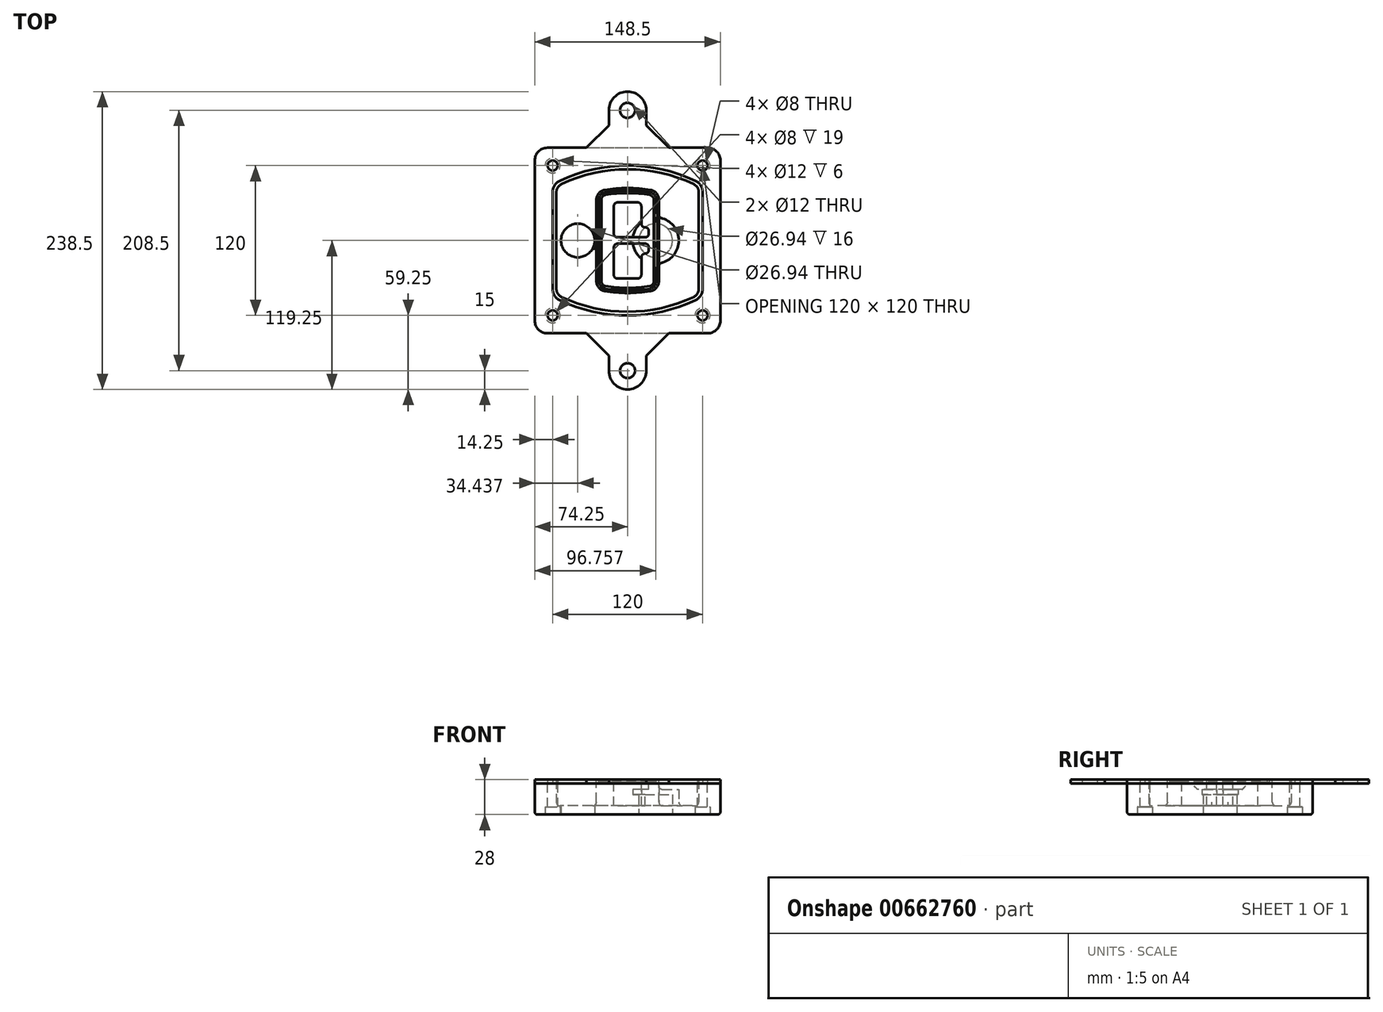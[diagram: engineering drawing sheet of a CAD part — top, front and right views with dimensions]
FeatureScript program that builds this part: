
annotation { "Feature Type Name" : "Feature", "Feature Type Description" : "" }
export const myFeature = defineFeature(function(context is Context, id is Id, definition is map)
    precondition{}
    {
        {
            var Q0;
            Q0=qCreatedBy(makeId("Top.planeOp"),FACE);
            var sketch = newSketch(context, id + "F0", { "sketchPlane" : qUnion([Q0])});
            skPoint(sketch, "E0.rect.middle", {"position": v(0, 0) * mm});
            skLineSegment(sketch, "E1.bottom", {"start": v(-64.25, -74.25) * mm, "end": v(64.25, -74.25) * mm});
            skLineSegment(sketch, "E1.top", {"start": v(-64.25, 74.25) * mm, "end": v(64.25, 74.25) * mm});
            skLineSegment(sketch, "E1.left", {"start": v(-74.25, -64.25) * mm, "end": v(-74.25, 64.25) * mm});
            skLineSegment(sketch, "E1.right", {"start": v(74.25, -64.25) * mm, "end": v(74.25, 64.25) * mm});
            skLineSegment(sketch, "E2", {"start": v(-74.25, 74.25) * mm, "end": v(74.25, -74.25) * mm, "construction": true});
            skLineSegment(sketch, "E3", {"start": v(74.25, 74.25) * mm, "end": v(-74.25, -74.25) * mm, "construction": true});
            skCircle(sketch, "E4", {"center": v(-60, 60) * mm, "radius": 4 * mm});
            skCircle(sketch, "E5", {"center": v(60, 60) * mm, "radius": 4 * mm});
            skCircle(sketch, "E6", {"center": v(60, -60) * mm, "radius": 4 * mm});
            skCircle(sketch, "E7", {"center": v(-60, -60) * mm, "radius": 4 * mm});
            skLineSegment(sketch, "E8", {"start": v(-60, 60) * mm, "end": v(60, 60) * mm, "construction": true});
            skLineSegment(sketch, "E9", {"start": v(60, 60) * mm, "end": v(60, -60) * mm, "construction": true});
            skLineSegment(sketch, "E10", {"start": v(60, -60) * mm, "end": v(-60, -60) * mm, "construction": true});
            skLineSegment(sketch, "E11", {"start": v(-60, -60) * mm, "end": v(-60, 60) * mm, "construction": true});
            skLineSegment(sketch, "E12", {"start": v(-60, 38.83) * mm, "end": v(-60, -38.83) * mm});
            skLineSegment(sketch, "E13", {"start": v(60, 38.83) * mm, "end": v(60, -38.83) * mm});
            skArc(sketch, "E14", {"start": v(54.26, 47.88) * mm, "mid": v(0, 60) * mm, "end": v(-54.26, 47.88) * mm});
            skArc(sketch, "E15", {"start": v(-54.26, -47.88) * mm, "mid": v(0, -60) * mm, "end": v(54.26, -47.88) * mm});
            skLineSegment(sketch, "E16", {"start": v(-60, 0) * mm, "end": v(60, 0) * mm, "construction": true});
            skPoint(sketch, "E17.visualSharp", {"position": v(-60, -45) * mm});
            skArc(sketch, "E17.filletArc", {"start": v(-60, -38.83) * mm, "mid": v(-58.44, -44.2) * mm, "end": v(-54.26, -47.88) * mm});
            skPoint(sketch, "E18.visualSharp", {"position": v(-60, 45) * mm});
            skArc(sketch, "E18.filletArc", {"start": v(-54.26, 47.88) * mm, "mid": v(-58.44, 44.2) * mm, "end": v(-60, 38.83) * mm});
            skPoint(sketch, "E19.visualSharp", {"position": v(60, 45) * mm});
            skArc(sketch, "E19.filletArc", {"start": v(60, 38.83) * mm, "mid": v(58.44, 44.2) * mm, "end": v(54.26, 47.88) * mm});
            skPoint(sketch, "E20.visualSharp", {"position": v(60, -45) * mm});
            skArc(sketch, "E20.filletArc", {"start": v(54.26, -47.88) * mm, "mid": v(58.44, -44.2) * mm, "end": v(60, -38.83) * mm});
            skPoint(sketch, "E21.visualSharp", {"position": v(-74.25, 74.25) * mm});
            skArc(sketch, "E21.filletArc", {"start": v(-64.25, 74.25) * mm, "mid": v(-71.32, 71.32) * mm, "end": v(-74.25, 64.25) * mm});
            skPoint(sketch, "E22.visualSharp", {"position": v(74.25, 74.25) * mm});
            skArc(sketch, "E22.filletArc", {"start": v(74.25, 64.25) * mm, "mid": v(71.32, 71.32) * mm, "end": v(64.25, 74.25) * mm});
            skPoint(sketch, "E23.visualSharp", {"position": v(74.25, -74.25) * mm});
            skArc(sketch, "E23.filletArc", {"start": v(64.25, -74.25) * mm, "mid": v(71.32, -71.32) * mm, "end": v(74.25, -64.25) * mm});
            skPoint(sketch, "E24.visualSharp", {"position": v(-74.25, -74.25) * mm});
            skArc(sketch, "E24.filletArc", {"start": v(-74.25, -64.25) * mm, "mid": v(-71.32, -71.32) * mm, "end": v(-64.25, -74.25) * mm});
            skArc(sketch, "E25.0", {"start": v(57, 38.83) * mm, "mid": v(55.9, 42.58) * mm, "end": v(52.98, 45.17) * mm});
            skLineSegment(sketch, "E25.1", {"start": v(57, 38.83) * mm, "end": v(57, -38.83) * mm});
            skArc(sketch, "E25.2", {"start": v(52.98, -45.17) * mm, "mid": v(55.9, -42.58) * mm, "end": v(57, -38.83) * mm});
            skArc(sketch, "E25.3", {"start": v(-52.98, -45.17) * mm, "mid": v(0, -57) * mm, "end": v(52.98, -45.17) * mm});
            skArc(sketch, "E25.4", {"start": v(-57, -38.83) * mm, "mid": v(-55.9, -42.58) * mm, "end": v(-52.98, -45.17) * mm});
            skArc(sketch, "E25.5", {"start": v(52.98, 45.17) * mm, "mid": v(0, 57) * mm, "end": v(-52.98, 45.17) * mm});
            skLineSegment(sketch, "E25.6", {"start": v(-57, 38.83) * mm, "end": v(-57, -38.83) * mm});
            skArc(sketch, "E25.7", {"start": v(-52.98, 45.17) * mm, "mid": v(-55.9, 42.58) * mm, "end": v(-57, 38.83) * mm});
            skArc(sketch, "E26.0", {"start": v(-55.96, 51.5) * mm, "mid": v(-61.82, 46.33) * mm, "end": v(-64, 38.83) * mm});
            skArc(sketch, "E26.1", {"start": v(55.96, 51.5) * mm, "mid": v(0, 64) * mm, "end": v(-55.96, 51.5) * mm});
            skArc(sketch, "E26.2", {"start": v(64, 38.83) * mm, "mid": v(61.82, 46.33) * mm, "end": v(55.96, 51.5) * mm});
            skLineSegment(sketch, "E26.3", {"start": v(64, 38.83) * mm, "end": v(64, -38.83) * mm});
            skArc(sketch, "E26.4", {"start": v(55.96, -51.5) * mm, "mid": v(61.82, -46.33) * mm, "end": v(64, -38.83) * mm});
            skLineSegment(sketch, "E26.5", {"start": v(-64, 38.83) * mm, "end": v(-64, -38.83) * mm});
            skArc(sketch, "E26.6", {"start": v(-55.96, -51.5) * mm, "mid": v(0, -64) * mm, "end": v(55.96, -51.5) * mm});
            skArc(sketch, "E26.7", {"start": v(-64, -38.83) * mm, "mid": v(-61.82, -46.33) * mm, "end": v(-55.96, -51.5) * mm});
            skSolve(sketch);
        }
        {
            var Q0;
            Q0=makeQuery(id+"F0.imprint","IMPRINT",FACE,{"disambiguationData":[TD([[makeQuery(id+"F0.imprint","IMPRINT",EDGE,{"derivedFrom":sQuery(id+"F0.wireOp",EDGE,"E1.bottom")}),1.0]])]});
            var Q1;
            Q1=makeQuery(id+"F0.imprint","IMPRINT",FACE,{"disambiguationData":[TD([[makeQuery(id+"F0.imprint","IMPRINT",EDGE,{"derivedFrom":sQuery(id+"F0.wireOp",EDGE,"E12")}),1.0]])]});
            var Q2;
            Q2=makeQuery(id+"F0.imprint","IMPRINT",FACE,{"disambiguationData":[TD([[makeQuery(id+"F0.imprint","IMPRINT",EDGE,{"derivedFrom":sQuery(id+"F0.wireOp",EDGE,"E25.0")}),1.0]])]});
            var Q3;
            Q3=makeQuery(id+"F0.imprint","IMPRINT",FACE,{"disambiguationData":[TD([[makeQuery(id+"F0.imprint","IMPRINT",EDGE,{"derivedFrom":sQuery(id+"F0.wireOp",EDGE,"E12")}),-1.0]])]});
            extrude(context, id + "F1", {"entities" : qUnion([Q0, Q1, Q2, Q3]), "oppositeDirection" : true, "depth" : 25 * mm});
        }
        {
            var Q0;
            Q0=makeQuery(id+"F0.imprint","IMPRINT",FACE,{"disambiguationData":[TD([[makeQuery(id+"F0.imprint","IMPRINT",EDGE,{"derivedFrom":sQuery(id+"F0.wireOp",EDGE,"E12")}),1.0]])]});
            extrude(context, id + "F2", {"entities" : qUnion([Q0]), "operationType" : NewBodyOperationType.ADD, "depth" : 3 * mm});
        }
        {
            var Q0;
            Q0=makeQuery(id+"F0.imprint","IMPRINT",FACE,{"disambiguationData":[TD([[makeQuery(id+"F0.imprint","IMPRINT",EDGE,{"derivedFrom":sQuery(id+"F0.wireOp",EDGE,"E25.0")}),1.0]])]});
            extrude(context, id + "F3", {"entities" : qUnion([Q0]), "operationType" : NewBodyOperationType.REMOVE, "oppositeDirection" : true, "depth" : 18 * mm});
        }
        {
            var Q0;
            Q0=makeQuery(id+"F2.opExtrude","CAP_FACE",FACE,{"disambiguationData":[OSD([sQuery(id+"F0.wireOp",EDGE,"E12"),sQuery(id+"F0.wireOp",EDGE,"E13"),sQuery(id+"F0.wireOp",EDGE,"E14"),sQuery(id+"F0.wireOp",EDGE,"E15"),sQuery(id+"F0.wireOp",EDGE,"E17.filletArc"),sQuery(id+"F0.wireOp",EDGE,"E18.filletArc"),sQuery(id+"F0.wireOp",EDGE,"E19.filletArc"),sQuery(id+"F0.wireOp",EDGE,"E20.filletArc"),sQuery(id+"F0.wireOp",EDGE,"E25.0"),sQuery(id+"F0.wireOp",EDGE,"E25.1"),sQuery(id+"F0.wireOp",EDGE,"E25.2"),sQuery(id+"F0.wireOp",EDGE,"E25.3"),sQuery(id+"F0.wireOp",EDGE,"E25.4"),sQuery(id+"F0.wireOp",EDGE,"E25.5"),sQuery(id+"F0.wireOp",EDGE,"E25.6"),sQuery(id+"F0.wireOp",EDGE,"E25.7")])],"isStart":false});
            var sketch = newSketch(context, id + "F4", { "sketchPlane" : qUnion([Q0])});
            skArc(sketch, "E27.0", {"start": v(-18.34, -40.45) * mm, "mid": v(0, -42) * mm, "end": v(18.34, -40.45) * mm});
            skArc(sketch, "E28.0", {"start": v(18.34, 40.45) * mm, "mid": v(0, 42) * mm, "end": v(-18.34, 40.45) * mm});
            skLineSegment(sketch, "E29", {"start": v(-25, 32.57) * mm, "end": v(-25, -32.57) * mm});
            skLineSegment(sketch, "E30", {"start": v(25, 32.57) * mm, "end": v(25, -32.57) * mm});
            skLineSegment(sketch, "E31", {"start": v(-25, 39.1) * mm, "end": v(25, 39.1) * mm, "construction": true});
            skLineSegment(sketch, "E32", {"start": v(-25, -39.1) * mm, "end": v(25, -39.1) * mm, "construction": true});
            skPoint(sketch, "E33.visualSharp", {"position": v(-25, 39.1) * mm});
            skArc(sketch, "E33.filletArc", {"start": v(-18.34, 40.45) * mm, "mid": v(-23.11, 37.73) * mm, "end": v(-25, 32.57) * mm});
            skPoint(sketch, "E34.visualSharp", {"position": v(25, 39.1) * mm});
            skArc(sketch, "E34.filletArc", {"start": v(25, 32.57) * mm, "mid": v(23.11, 37.73) * mm, "end": v(18.34, 40.45) * mm});
            skPoint(sketch, "E35.visualSharp", {"position": v(25, -39.1) * mm});
            skArc(sketch, "E35.filletArc", {"start": v(18.34, -40.45) * mm, "mid": v(23.11, -37.73) * mm, "end": v(25, -32.57) * mm});
            skPoint(sketch, "E36.visualSharp", {"position": v(-25, -39.1) * mm});
            skArc(sketch, "E36.filletArc", {"start": v(-25, -32.57) * mm, "mid": v(-23.11, -37.73) * mm, "end": v(-18.34, -40.45) * mm});
            skArc(sketch, "E37.0", {"start": v(52.98, 45.17) * mm, "mid": v(0, 57) * mm, "end": v(-52.98, 45.17) * mm});
            skArc(sketch, "E37.1", {"start": v(-52.98, 45.17) * mm, "mid": v(-55.9, 42.58) * mm, "end": v(-57, 38.83) * mm});
            skLineSegment(sketch, "E37.2", {"start": v(-57, 38.83) * mm, "end": v(-57, -38.83) * mm});
            skArc(sketch, "E37.3", {"start": v(-57, -38.83) * mm, "mid": v(-55.9, -42.58) * mm, "end": v(-52.98, -45.17) * mm});
            skArc(sketch, "E37.4", {"start": v(-52.98, -45.17) * mm, "mid": v(0, -57) * mm, "end": v(52.98, -45.17) * mm});
            skArc(sketch, "E37.5", {"start": v(52.98, -45.17) * mm, "mid": v(55.9, -42.58) * mm, "end": v(57, -38.83) * mm});
            skLineSegment(sketch, "E37.6", {"start": v(57, 38.83) * mm, "end": v(57, -38.83) * mm});
            skArc(sketch, "E37.7", {"start": v(57, 38.83) * mm, "mid": v(55.9, 42.58) * mm, "end": v(52.98, 45.17) * mm});
            skLineSegment(sketch, "E38.0", {"start": v(23, 32.57) * mm, "end": v(23, -32.57) * mm});
            skArc(sketch, "E38.1", {"start": v(18, -38.48) * mm, "mid": v(21.58, -36.44) * mm, "end": v(23, -32.57) * mm});
            skArc(sketch, "E38.2", {"start": v(-18, -38.48) * mm, "mid": v(0, -40) * mm, "end": v(18, -38.48) * mm});
            skArc(sketch, "E38.3", {"start": v(-23, -32.57) * mm, "mid": v(-21.58, -36.44) * mm, "end": v(-18, -38.48) * mm});
            skLineSegment(sketch, "E38.4", {"start": v(-23, 32.57) * mm, "end": v(-23, -32.57) * mm});
            skArc(sketch, "E38.5", {"start": v(23, 32.57) * mm, "mid": v(21.58, 36.44) * mm, "end": v(18, 38.48) * mm});
            skArc(sketch, "E38.6", {"start": v(-18, 38.48) * mm, "mid": v(-21.58, 36.44) * mm, "end": v(-23, 32.57) * mm});
            skArc(sketch, "E38.7", {"start": v(18, 38.48) * mm, "mid": v(0, 40) * mm, "end": v(-18, 38.48) * mm});
            skArc(sketch, "E39.0", {"start": v(21, 32.57) * mm, "mid": v(20.06, 35.15) * mm, "end": v(17.67, 36.5) * mm});
            skLineSegment(sketch, "E39.1", {"start": v(21, 32.57) * mm, "end": v(21, -32.57) * mm});
            skArc(sketch, "E39.2", {"start": v(17.67, -36.5) * mm, "mid": v(20.06, -35.15) * mm, "end": v(21, -32.57) * mm});
            skArc(sketch, "E39.3", {"start": v(-17.67, -36.5) * mm, "mid": v(0, -38) * mm, "end": v(17.67, -36.5) * mm});
            skArc(sketch, "E39.4", {"start": v(-21, -32.57) * mm, "mid": v(-20.06, -35.15) * mm, "end": v(-17.67, -36.5) * mm});
            skArc(sketch, "E39.5", {"start": v(17.67, 36.5) * mm, "mid": v(0, 38) * mm, "end": v(-17.67, 36.5) * mm});
            skLineSegment(sketch, "E39.6", {"start": v(-21, 32.57) * mm, "end": v(-21, -32.57) * mm});
            skArc(sketch, "E39.7", {"start": v(-17.67, 36.5) * mm, "mid": v(-20.06, 35.15) * mm, "end": v(-21, 32.57) * mm});
            skLineSegment(sketch, "E40", {"start": v(-25, 0) * mm, "end": v(25, 0) * mm, "construction": true});
            skLineSegment(sketch, "E41", {"start": v(-11, 5.5) * mm, "end": v(-11, 27.5) * mm});
            skLineSegment(sketch, "E42", {"start": v(-8, 30.5) * mm, "end": v(8, 30.5) * mm});
            skLineSegment(sketch, "E43", {"start": v(11, 27.5) * mm, "end": v(11, 13.5) * mm});
            skLineSegment(sketch, "E44", {"start": v(14, 10.5) * mm, "end": v(14, 10.5) * mm});
            skLineSegment(sketch, "E45", {"start": v(17, 7.5) * mm, "end": v(17, 5.5) * mm});
            skLineSegment(sketch, "E46", {"start": v(14, 2.5) * mm, "end": v(-8, 2.5) * mm});
            skPoint(sketch, "E47.visualSharp", {"position": v(-11, 30.5) * mm});
            skArc(sketch, "E47.filletArc", {"start": v(-8, 30.5) * mm, "mid": v(-10.12, 29.62) * mm, "end": v(-11, 27.5) * mm});
            skPoint(sketch, "E48.visualSharp", {"position": v(11, 30.5) * mm});
            skArc(sketch, "E48.filletArc", {"start": v(11, 27.5) * mm, "mid": v(10.12, 29.62) * mm, "end": v(8, 30.5) * mm});
            skPoint(sketch, "E49.visualSharp", {"position": v(11, 10.5) * mm});
            skArc(sketch, "E49.filletArc", {"start": v(11, 13.5) * mm, "mid": v(11.88, 11.38) * mm, "end": v(14, 10.5) * mm});
            skPoint(sketch, "E50.visualSharp", {"position": v(17, 10.5) * mm});
            skArc(sketch, "E50.filletArc", {"start": v(17, 7.5) * mm, "mid": v(16.12, 9.62) * mm, "end": v(14, 10.5) * mm});
            skPoint(sketch, "E51.visualSharp", {"position": v(17, 2.5) * mm});
            skArc(sketch, "E51.filletArc", {"start": v(14, 2.5) * mm, "mid": v(16.12, 3.38) * mm, "end": v(17, 5.5) * mm});
            skPoint(sketch, "E52.visualSharp", {"position": v(-11, 2.5) * mm});
            skArc(sketch, "E52.filletArc", {"start": v(-11, 5.5) * mm, "mid": v(-10.12, 3.38) * mm, "end": v(-8, 2.5) * mm});
            skLineSegment(sketch, "E53.0.MirrorCS", {"start": v(14, -2.5) * mm, "end": v(-8, -2.5) * mm});
            skArc(sketch, "E54.0.MirrorCS", {"start": v(-11, -5.5) * mm, "mid": v(-10.12, -3.38) * mm, "end": v(-8, -2.5) * mm});
            skLineSegment(sketch, "E55.0.MirrorCS", {"start": v(-11, -5.5) * mm, "end": v(-11, -27.5) * mm});
            skArc(sketch, "E56.0.MirrorCS", {"start": v(-8, -30.5) * mm, "mid": v(-10.12, -29.62) * mm, "end": v(-11, -27.5) * mm});
            skLineSegment(sketch, "E57.0.MirrorCS", {"start": v(-8, -30.5) * mm, "end": v(8, -30.5) * mm});
            skArc(sketch, "E58.0.MirrorCS", {"start": v(11, -27.5) * mm, "mid": v(10.12, -29.62) * mm, "end": v(8, -30.5) * mm});
            skLineSegment(sketch, "E59.0.MirrorCS", {"start": v(11, -27.5) * mm, "end": v(11, -13.5) * mm});
            skArc(sketch, "E60.0.MirrorCS", {"start": v(11, -13.5) * mm, "mid": v(11.88, -11.38) * mm, "end": v(14, -10.5) * mm});
            skArc(sketch, "E61.0.MirrorCS", {"start": v(17, -7.5) * mm, "mid": v(16.12, -9.62) * mm, "end": v(14, -10.5) * mm});
            skLineSegment(sketch, "E62.0.MirrorCS", {"start": v(17, -7.5) * mm, "end": v(17, -5.5) * mm});
            skArc(sketch, "E63.0.MirrorCS", {"start": v(14, -2.5) * mm, "mid": v(16.12, -3.38) * mm, "end": v(17, -5.5) * mm});
            skSolve(sketch);
        }
        {
            var Q0;
            Q0=makeQuery(id+"F4.imprint","IMPRINT",FACE,{"disambiguationData":[TD([[makeQuery(id+"F4.imprint","IMPRINT",EDGE,{"derivedFrom":sQuery(id+"F4.wireOp",EDGE,"E27.0")}),1.0]])]});
            var Q1;
            Q1=makeQuery(id+"F4.imprint","IMPRINT",FACE,{"disambiguationData":[TD([[makeQuery(id+"F4.imprint","IMPRINT",EDGE,{"derivedFrom":sQuery(id+"F4.wireOp",EDGE,"E38.0")}),-1.0]])]});
            var Q2;
            Q2=makeQuery(id+"F4.imprint","IMPRINT",FACE,{"disambiguationData":[TD([[makeQuery(id+"F4.imprint","IMPRINT",EDGE,{"derivedFrom":sQuery(id+"F4.wireOp",EDGE,"E39.0")}),1.0]])]});
            extrude(context, id + "F5", {"entities" : qUnion([Q0, Q1, Q2]), "operationType" : NewBodyOperationType.ADD, "endBound" : BoundingType.UP_TO_NEXT, "oppositeDirection" : true, "depth" : 25 * mm});
        }
        {
            var Q0;
            Q0=makeQuery(id+"F4.imprint","IMPRINT",FACE,{"disambiguationData":[TD([[makeQuery(id+"F4.imprint","IMPRINT",EDGE,{"derivedFrom":sQuery(id+"F4.wireOp",EDGE,"E38.0")}),-1.0]])]});
            extrude(context, id + "F6", {"entities" : qUnion([Q0]), "operationType" : NewBodyOperationType.REMOVE, "oppositeDirection" : true, "depth" : 2 * mm});
        }
        {
            var Q0;
            Q0=makeQuery(id+"F1.opExtrude","CAP_FACE",FACE,{"disambiguationData":[OSD([sQuery(id+"F0.wireOp",EDGE,"E1.bottom"),sQuery(id+"F0.wireOp",EDGE,"E1.top"),sQuery(id+"F0.wireOp",EDGE,"E1.left"),sQuery(id+"F0.wireOp",EDGE,"E1.right"),sQuery(id+"F0.wireOp",EDGE,"E4"),sQuery(id+"F0.wireOp",EDGE,"E5"),sQuery(id+"F0.wireOp",EDGE,"E6"),sQuery(id+"F0.wireOp",EDGE,"E7"),sQuery(id+"F0.wireOp",EDGE,"E21.filletArc"),sQuery(id+"F0.wireOp",EDGE,"E22.filletArc"),sQuery(id+"F0.wireOp",EDGE,"E23.filletArc"),sQuery(id+"F0.wireOp",EDGE,"E24.filletArc")])],"isStart":false});
            var sketch = newSketch(context, id + "F7", { "sketchPlane" : qUnion([Q0])});
            skCircle(sketch, "E64", {"center": v(22.5, 0) * mm, "radius": 13.47 * mm});
            skCircle(sketch, "E65", {"center": v(-39.81, 0) * mm, "radius": 13.47 * mm});
            skLineSegment(sketch, "E66", {"start": v(74.25, 0) * mm, "end": v(-74.25, 0) * mm});
            skCircle(sketch, "E67", {"center": v(22.5, 0) * mm, "radius": 18.47 * mm});
            skCircle(sketch, "E68", {"center": v(60, -60) * mm, "radius": 6 * mm});
            skCircle(sketch, "E69", {"center": v(-60, -60) * mm, "radius": 6 * mm});
            skCircle(sketch, "E70", {"center": v(-60, 60) * mm, "radius": 6 * mm});
            skCircle(sketch, "E71", {"center": v(60, 60) * mm, "radius": 6 * mm});
            skSolve(sketch);
        }
        {
            var Q0;
            {var subQ1=sQuery(id+"F7.wireOp",EDGE,"E66");var subQ4=sQuery(id+"F7.wireOp",EDGE,"E64");var subQ6=makeQuery(id+"F7.imprint","INTERSECT",VERTEX,{"disambiguationData":[OD(0.0)],"derivedFrom":[subQ4,subQ1]});Q0=makeQuery(id+"F7.imprint","IMPRINT",FACE,{"disambiguationData":[TD([[makeQuery(id+"F7.imprint","IMPRINT",EDGE,{"disambiguationData":[TD([[subQ6,-1.0]])],"derivedFrom":subQ4}),-1.0]])]});}
            var Q1;
            {var subQ0=sQuery(id+"F7.wireOp",EDGE,"E66");var subQ1=sQuery(id+"F7.wireOp",EDGE,"E64");var subQ3=makeQuery(id+"F7.imprint","INTERSECT",VERTEX,{"disambiguationData":[OD(0.0)],"derivedFrom":[subQ1,subQ0]});Q1=makeQuery(id+"F7.imprint","IMPRINT",FACE,{"disambiguationData":[TD([[makeQuery(id+"F7.imprint","IMPRINT",EDGE,{"disambiguationData":[TD([[subQ3,-1.0]])],"derivedFrom":subQ1}),1.0]])]});}
            var Q2;
            {var subQ0=sQuery(id+"F7.wireOp",EDGE,"E66");var subQ1=sQuery(id+"F7.wireOp",EDGE,"E64");var subQ3=makeQuery(id+"F7.imprint","INTERSECT",VERTEX,{"disambiguationData":[OD(0.0)],"derivedFrom":[subQ1,subQ0]});Q2=makeQuery(id+"F7.imprint","IMPRINT",FACE,{"disambiguationData":[TD([[makeQuery(id+"F7.imprint","IMPRINT",EDGE,{"disambiguationData":[TD([[subQ3,1.0]])],"derivedFrom":subQ1}),1.0]])]});}
            var Q3;
            {var subQ1=sQuery(id+"F7.wireOp",EDGE,"E66");var subQ4=sQuery(id+"F7.wireOp",EDGE,"E64");var subQ6=makeQuery(id+"F7.imprint","INTERSECT",VERTEX,{"disambiguationData":[OD(0.0)],"derivedFrom":[subQ4,subQ1]});Q3=makeQuery(id+"F7.imprint","IMPRINT",FACE,{"disambiguationData":[TD([[makeQuery(id+"F7.imprint","IMPRINT",EDGE,{"disambiguationData":[TD([[subQ6,1.0]])],"derivedFrom":subQ4}),-1.0]])]});}
            extrude(context, id + "F8", {"entities" : qUnion([Q0, Q1, Q2, Q3]), "operationType" : NewBodyOperationType.ADD, "oppositeDirection" : true, "depth" : 20 * mm});
        }
        {
            var Q0;
            {var subQ0=sQuery(id+"F7.wireOp",EDGE,"E66");var subQ1=sQuery(id+"F7.wireOp",EDGE,"E64");var subQ3=makeQuery(id+"F7.imprint","INTERSECT",VERTEX,{"disambiguationData":[OD(0.0)],"derivedFrom":[subQ1,subQ0]});Q0=makeQuery(id+"F7.imprint","IMPRINT",FACE,{"disambiguationData":[TD([[makeQuery(id+"F7.imprint","IMPRINT",EDGE,{"disambiguationData":[TD([[subQ3,-1.0]])],"derivedFrom":subQ1}),1.0]])]});}
            var Q1;
            {var subQ0=sQuery(id+"F7.wireOp",EDGE,"E66");var subQ1=sQuery(id+"F7.wireOp",EDGE,"E64");var subQ3=makeQuery(id+"F7.imprint","INTERSECT",VERTEX,{"disambiguationData":[OD(0.0)],"derivedFrom":[subQ1,subQ0]});Q1=makeQuery(id+"F7.imprint","IMPRINT",FACE,{"disambiguationData":[TD([[makeQuery(id+"F7.imprint","IMPRINT",EDGE,{"disambiguationData":[TD([[subQ3,1.0]])],"derivedFrom":subQ1}),1.0]])]});}
            extrude(context, id + "F9", {"entities" : qUnion([Q0, Q1]), "operationType" : NewBodyOperationType.REMOVE, "oppositeDirection" : true, "depth" : 16 * mm});
        }
        {
            var Q0;
            {var subQ0=sQuery(id+"F7.wireOp",EDGE,"E66");var subQ1=sQuery(id+"F7.wireOp",EDGE,"E65");var subQ3=makeQuery(id+"F7.imprint","INTERSECT",VERTEX,{"disambiguationData":[OD(0.0)],"derivedFrom":[subQ1,subQ0]});Q0=makeQuery(id+"F7.imprint","IMPRINT",FACE,{"disambiguationData":[TD([[makeQuery(id+"F7.imprint","IMPRINT",EDGE,{"disambiguationData":[TD([[subQ3,-1.0]])],"derivedFrom":subQ1}),1.0]])]});}
            var Q1;
            {var subQ0=sQuery(id+"F7.wireOp",EDGE,"E66");var subQ1=sQuery(id+"F7.wireOp",EDGE,"E65");var subQ3=makeQuery(id+"F7.imprint","INTERSECT",VERTEX,{"disambiguationData":[OD(0.0)],"derivedFrom":[subQ1,subQ0]});Q1=makeQuery(id+"F7.imprint","IMPRINT",FACE,{"disambiguationData":[TD([[makeQuery(id+"F7.imprint","IMPRINT",EDGE,{"disambiguationData":[TD([[subQ3,1.0]])],"derivedFrom":subQ1}),1.0]])]});}
            extrude(context, id + "F10", {"entities" : qUnion([Q0, Q1]), "operationType" : NewBodyOperationType.REMOVE, "oppositeDirection" : true, "depth" : 25 * mm});
        }
        {
            var Q0;
            Q0=makeQuery(id+"F7.imprint","IMPRINT",FACE,{"disambiguationData":[TD([[makeQuery(id+"F7.imprint","IMPRINT",EDGE,{"derivedFrom":sQuery(id+"F7.wireOp",EDGE,"E68")}),1.0]])]});
            var Q1;
            Q1=makeQuery(id+"F7.imprint","IMPRINT",FACE,{"disambiguationData":[TD([[makeQuery(id+"F7.imprint","IMPRINT",EDGE,{"derivedFrom":makeQuery(id+"F1.opExtrude","CAP_EDGE",EDGE,{"disambiguationData":[OSD([sQuery(id+"F0.wireOp",EDGE,"E5")])],"isStart":false})}),-1.0]])]});
            var Q2;
            Q2=makeQuery(id+"F7.imprint","IMPRINT",FACE,{"disambiguationData":[TD([[makeQuery(id+"F7.imprint","IMPRINT",EDGE,{"derivedFrom":sQuery(id+"F7.wireOp",EDGE,"E69")}),1.0]])]});
            var Q3;
            Q3=makeQuery(id+"F7.imprint","IMPRINT",FACE,{"disambiguationData":[TD([[makeQuery(id+"F7.imprint","IMPRINT",EDGE,{"derivedFrom":makeQuery(id+"F1.opExtrude","CAP_EDGE",EDGE,{"disambiguationData":[OSD([sQuery(id+"F0.wireOp",EDGE,"E4")])],"isStart":false})}),-1.0]])]});
            var Q4;
            Q4=makeQuery(id+"F7.imprint","IMPRINT",FACE,{"disambiguationData":[TD([[makeQuery(id+"F7.imprint","IMPRINT",EDGE,{"derivedFrom":sQuery(id+"F7.wireOp",EDGE,"E70")}),1.0]])]});
            var Q5;
            Q5=makeQuery(id+"F7.imprint","IMPRINT",FACE,{"disambiguationData":[TD([[makeQuery(id+"F7.imprint","IMPRINT",EDGE,{"derivedFrom":makeQuery(id+"F1.opExtrude","CAP_EDGE",EDGE,{"disambiguationData":[OSD([sQuery(id+"F0.wireOp",EDGE,"E7")])],"isStart":false})}),-1.0]])]});
            var Q6;
            Q6=makeQuery(id+"F7.imprint","IMPRINT",FACE,{"disambiguationData":[TD([[makeQuery(id+"F7.imprint","IMPRINT",EDGE,{"derivedFrom":sQuery(id+"F7.wireOp",EDGE,"E71")}),1.0]])]});
            var Q7;
            Q7=makeQuery(id+"F7.imprint","IMPRINT",FACE,{"disambiguationData":[TD([[makeQuery(id+"F7.imprint","IMPRINT",EDGE,{"derivedFrom":makeQuery(id+"F1.opExtrude","CAP_EDGE",EDGE,{"disambiguationData":[OSD([sQuery(id+"F0.wireOp",EDGE,"E6")])],"isStart":false})}),-1.0]])]});
            extrude(context, id + "F11", {"entities" : qUnion([Q0, Q1, Q2, Q3, Q4, Q5, Q6, Q7]), "operationType" : NewBodyOperationType.REMOVE, "oppositeDirection" : true, "depth" : 6 * mm});
        }
        {
            var Q0;
            Q0=makeQuery(id+"F9.boolean.opBoolean","COPY",FACE,{"derivedFrom":makeQuery(id+"F9.opExtrude","CAP_FACE",FACE,{"disambiguationData":[OSD([sQuery(id+"F7.wireOp",EDGE,"E64")])],"isStart":false})});
            var sketch = newSketch(context, id + "F12", { "sketchPlane" : qUnion([Q0])});
            skArc(sketch, "E72.0", {"start": v(11, 14.45) * mm, "mid": v(6.45, 9.13) * mm, "end": v(4.2, 2.5) * mm});
            skArc(sketch, "E72.1", {"start": v(4.2, -2.5) * mm, "mid": v(6.45, -9.13) * mm, "end": v(11, -14.45) * mm});
            skLineSegment(sketch, "E73", {"start": v(4.2, -2.5) * mm, "end": v(14, -2.5) * mm});
            skLineSegment(sketch, "E74.0", {"start": v(14, 2.5) * mm, "end": v(4.2, 2.5) * mm});
            skArc(sketch, "E74.1", {"start": v(14, 2.5) * mm, "mid": v(16.12, 3.38) * mm, "end": v(17, 5.5) * mm});
            skLineSegment(sketch, "E74.2", {"start": v(17, 7.5) * mm, "end": v(17, 5.5) * mm});
            skArc(sketch, "E74.3", {"start": v(17, 7.5) * mm, "mid": v(16.12, 9.62) * mm, "end": v(14, 10.5) * mm});
            skArc(sketch, "E74.4", {"start": v(11, 13.5) * mm, "mid": v(11.88, 11.38) * mm, "end": v(14, 10.5) * mm});
            skLineSegment(sketch, "E74.5", {"start": v(11, 14.45) * mm, "end": v(11, 13.5) * mm});
            skLineSegment(sketch, "E74.7", {"start": v(14, -2.5) * mm, "end": v(4.2, -2.5) * mm});
            skArc(sketch, "E74.8", {"start": v(14, -2.5) * mm, "mid": v(16.12, -3.38) * mm, "end": v(17, -5.5) * mm});
            skLineSegment(sketch, "E74.9", {"start": v(17, -7.5) * mm, "end": v(17, -5.5) * mm});
            skArc(sketch, "E74.10", {"start": v(17, -7.5) * mm, "mid": v(16.12, -9.62) * mm, "end": v(14, -10.5) * mm});
            skArc(sketch, "E74.11", {"start": v(11, -13.5) * mm, "mid": v(11.88, -11.38) * mm, "end": v(14, -10.5) * mm});
            skLineSegment(sketch, "E74.12", {"start": v(11, -14.45) * mm, "end": v(11, -13.5) * mm});
            skPoint(sketch, "E75.orphan", {"position": v(11, -27.5) * mm});
            skPoint(sketch, "E76.orphan", {"position": v(-8, -2.5) * mm});
            skPoint(sketch, "E77.orphan", {"position": v(-8, 2.5) * mm});
            skPoint(sketch, "E78.orphan", {"position": v(11, 27.5) * mm});
            skSolve(sketch);
        }
        {
            var Q0;
            {var subQ7=sQuery(id+"F12.wireOp",EDGE,"E72.0");var subQ14=sQuery(id+"F12.wireOp",EDGE,"E72.1");var subQ16=sQuery(id+"F12.wireOp",EDGE,"E74.1");var subQ18=sQuery(id+"F12.wireOp",EDGE,"E74.8");Q0=qUnion([makeQuery(id+"F12.imprint","IMPRINT",FACE,{"disambiguationData":[TD([[makeQuery(id+"F12.imprint","IMPRINT",EDGE,{"derivedFrom":subQ7}),1.0]])]}),makeQuery(id+"F12.imprint","IMPRINT",FACE,{"disambiguationData":[TD([[makeQuery(id+"F12.imprint","IMPRINT",EDGE,{"derivedFrom":subQ14}),1.0]])]}),makeQuery(id+"F12.imprint","IMPRINT",FACE,{"disambiguationData":[TD([[makeQuery(id+"F12.imprint","IMPRINT",EDGE,{"derivedFrom":subQ16}),1.0]])]}),makeQuery(id+"F12.imprint","IMPRINT",FACE,{"disambiguationData":[TD([[makeQuery(id+"F12.imprint","IMPRINT",EDGE,{"derivedFrom":subQ18}),-1.0]])]})]);}
            var Q1;
            Q1=makeQuery(id+"F5.boolean.opBoolean","SPLIT",FACE,{"disambiguationData":[TD([makeQuery(id+"F5.opExtrude","SWEPT_FACE",FACE,{"disambiguationData":[OSD([sQuery(id+"F4.wireOp",EDGE,"E41")])]})])],"derivedFrom":makeQuery(id+"F3.boolean.opBoolean","COPY",FACE,{"derivedFrom":makeQuery(id+"F3.opExtrude","CAP_FACE",FACE,{"disambiguationData":[OSD([sQuery(id+"F0.wireOp",EDGE,"E25.0"),sQuery(id+"F0.wireOp",EDGE,"E25.1"),sQuery(id+"F0.wireOp",EDGE,"E25.2"),sQuery(id+"F0.wireOp",EDGE,"E25.3"),sQuery(id+"F0.wireOp",EDGE,"E25.4"),sQuery(id+"F0.wireOp",EDGE,"E25.5"),sQuery(id+"F0.wireOp",EDGE,"E25.6"),sQuery(id+"F0.wireOp",EDGE,"E25.7")])],"isStart":false})})});
            extrude(context, id + "F13", {"entities" : qUnion([Q0]), "operationType" : NewBodyOperationType.REMOVE, "endBound" : BoundingType.UP_TO_SURFACE, "endBoundEntityFace" : qUnion([Q1]), "depth" : 25 * mm});
        }
        {
            var Q0;
            Q0=makeQuery(id+"F3.boolean.opBoolean","COPY",EDGE,{"derivedFrom":makeQuery(id+"F3.opExtrude","CAP_EDGE",EDGE,{"disambiguationData":[OSD([sQuery(id+"F0.wireOp",EDGE,"E25.6")])],"isStart":false})});
            var Q1;
            Q1=makeQuery(id+"F8.boolean.opBoolean","INTERSECT",EDGE,{"derivedFrom":[makeQuery(id+"F5.opExtrude","SWEPT_FACE",FACE,{"disambiguationData":[OSD([sQuery(id+"F4.wireOp",EDGE,"E30")])]}),makeQuery(id+"F8.opExtrude","CAP_FACE",FACE,{"disambiguationData":[OSD([sQuery(id+"F7.wireOp",EDGE,"E67")])],"isStart":false})]});
            var Q2;
            Q2=makeQuery(id+"F8.boolean.opBoolean","INTERSECT",EDGE,{"disambiguationData":[OD(1.0)],"derivedFrom":[makeQuery(id+"F5.opExtrude","SWEPT_FACE",FACE,{"disambiguationData":[OSD([sQuery(id+"F4.wireOp",EDGE,"E30")])]}),makeQuery(id+"F8.opExtrude","SWEPT_FACE",FACE,{"disambiguationData":[OSD([sQuery(id+"F7.wireOp",EDGE,"E67")])]})]});
            var Q3;
            {var subQ0=sQuery(id+"F4.wireOp",EDGE,"E30");Q3=makeQuery(id+"F8.boolean.opBoolean","SPLIT",EDGE,{"disambiguationData":[TD([makeQuery(id+"F5.opExtrude","SWEPT_FACE",FACE,{"disambiguationData":[OSD([sQuery(id+"F4.wireOp",EDGE,"E35.filletArc")])]})])],"derivedFrom":makeQuery(id+"F5.opExtrude","CAP_EDGE",EDGE,{"disambiguationData":[OSD([subQ0])],"isStart":false})});}
            var Q4;
            {var subQ0=sQuery(id+"F0.wireOp",EDGE,"E25.7");var subQ1=sQuery(id+"F0.wireOp",EDGE,"E25.1");var subQ2=sQuery(id+"F0.wireOp",EDGE,"E25.6");var subQ3=sQuery(id+"F0.wireOp",EDGE,"E25.5");var subQ4=sQuery(id+"F0.wireOp",EDGE,"E25.4");var subQ5=sQuery(id+"F0.wireOp",EDGE,"E25.0");var subQ6=sQuery(id+"F0.wireOp",EDGE,"E25.2");var subQ7=sQuery(id+"F0.wireOp",EDGE,"E25.3");Q4=makeQuery(id+"F8.boolean.opBoolean","INTERSECT",EDGE,{"derivedFrom":[makeQuery(id+"F5.boolean.opBoolean","SPLIT",FACE,{"disambiguationData":[TD([makeQuery(id+"F2.opExtrude","SWEPT_FACE",FACE,{"disambiguationData":[OSD([subQ5])]})])],"derivedFrom":makeQuery(id+"F3.boolean.opBoolean","COPY",FACE,{"derivedFrom":makeQuery(id+"F3.opExtrude","CAP_FACE",FACE,{"disambiguationData":[OSD([subQ5,subQ1,subQ6,subQ7,subQ4,subQ3,subQ2,subQ0])],"isStart":false})})}),makeQuery(id+"F8.opExtrude","SWEPT_FACE",FACE,{"disambiguationData":[OSD([sQuery(id+"F7.wireOp",EDGE,"E67")])]})]});}
            var Q5;
            Q5=makeQuery(id+"F8.boolean.opBoolean","INTERSECT",EDGE,{"disambiguationData":[OD(0.0)],"derivedFrom":[makeQuery(id+"F5.opExtrude","SWEPT_FACE",FACE,{"disambiguationData":[OSD([sQuery(id+"F4.wireOp",EDGE,"E30")])]}),makeQuery(id+"F8.opExtrude","SWEPT_FACE",FACE,{"disambiguationData":[OSD([sQuery(id+"F7.wireOp",EDGE,"E67")])]})]});
            fillet(context, id + "F14", {"entities" : qUnion([Q0, Q1, Q2, Q3, Q4, Q5]), "radius" : 3 * mm, "tangentPropagation" : true, "allowEdgeOverflow" : false});
        }
        {
            var Q0;
            Q0=makeQuery(id+"F1.opExtrude","CAP_EDGE",EDGE,{"disambiguationData":[OSD([sQuery(id+"F0.wireOp",EDGE,"E1.bottom")])],"isStart":false});
            fillet(context, id + "F15", {"entities" : qUnion([Q0]), "radius" : 2 * mm, "tangentPropagation" : true, "allowEdgeOverflow" : false});
        }
        {
            var Q0;
            {var subQ0=sQuery(id+"F0.wireOp",EDGE,"E21.filletArc");var subQ1=sQuery(id+"F0.wireOp",EDGE,"E7");var subQ2=sQuery(id+"F0.wireOp",EDGE,"E6");var subQ3=sQuery(id+"F0.wireOp",EDGE,"E5");var subQ4=sQuery(id+"F0.wireOp",EDGE,"E4");var subQ5=sQuery(id+"F0.wireOp",EDGE,"E22.filletArc");var subQ6=sQuery(id+"F0.wireOp",EDGE,"E1.bottom");var subQ7=sQuery(id+"F0.wireOp",EDGE,"E1.right");var subQ8=sQuery(id+"F0.wireOp",EDGE,"E1.top");var subQ9=sQuery(id+"F0.wireOp",EDGE,"E1.left");var subQ10=sQuery(id+"F0.wireOp",EDGE,"E23.filletArc");var subQ11=sQuery(id+"F0.wireOp",EDGE,"E24.filletArc");Q0=makeQuery(id+"F2.boolean.opBoolean","SPLIT",FACE,{"disambiguationData":[TD([makeQuery(id+"F1.opExtrude","SWEPT_FACE",FACE,{"disambiguationData":[OSD([subQ6])]})])],"derivedFrom":makeQuery(id+"F1.opExtrude","CAP_FACE",FACE,{"disambiguationData":[OSD([subQ6,subQ8,subQ9,subQ7,subQ4,subQ3,subQ2,subQ1,subQ0,subQ5,subQ10,subQ11])],"isStart":true})});}
            var sketch = newSketch(context, id + "F16", { "sketchPlane" : qUnion([Q0])});
            skArc(sketch, "E79.0", {"start": v(-54.26, -47.88) * mm, "mid": v(0, -60) * mm, "end": v(54.26, -47.88) * mm});
            skLineSegment(sketch, "E79.1", {"start": v(-60, 38.83) * mm, "end": v(-60, -38.83) * mm});
            skLineSegment(sketch, "E79.2", {"start": v(60, 38.83) * mm, "end": v(60, -38.83) * mm});
            skArc(sketch, "E79.3", {"start": v(54.26, -47.88) * mm, "mid": v(58.44, -44.2) * mm, "end": v(60, -38.83) * mm});
            skLineSegment(sketch, "E79.4", {"start": v(-74.25, -64.25) * mm, "end": v(-74.25, 64.25) * mm});
            skLineSegment(sketch, "E79.5", {"start": v(-64.25, -74.25) * mm, "end": v(64.25, -74.25) * mm});
            skArc(sketch, "E79.6", {"start": v(-74.25, -64.25) * mm, "mid": v(-71.32, -71.32) * mm, "end": v(-64.25, -74.25) * mm});
            skArc(sketch, "E79.7", {"start": v(64.25, -74.25) * mm, "mid": v(71.32, -71.32) * mm, "end": v(74.25, -64.25) * mm});
            skLineSegment(sketch, "E79.8", {"start": v(74.25, -64.25) * mm, "end": v(74.25, 64.25) * mm});
            skArc(sketch, "E79.9", {"start": v(74.25, 64.25) * mm, "mid": v(71.32, 71.32) * mm, "end": v(64.25, 74.25) * mm});
            skArc(sketch, "E79.11", {"start": v(54.26, 47.88) * mm, "mid": v(0, 60) * mm, "end": v(-54.26, 47.88) * mm});
            skArc(sketch, "E79.12", {"start": v(-54.26, 47.88) * mm, "mid": v(-58.44, 44.2) * mm, "end": v(-60, 38.83) * mm});
            skArc(sketch, "E79.13", {"start": v(60, 38.83) * mm, "mid": v(58.44, 44.2) * mm, "end": v(54.26, 47.88) * mm});
            skArc(sketch, "E79.14", {"start": v(-64.25, 74.25) * mm, "mid": v(-71.32, 71.32) * mm, "end": v(-74.25, 64.25) * mm});
            skArc(sketch, "E79.15", {"start": v(-60, -38.83) * mm, "mid": v(-58.44, -44.2) * mm, "end": v(-54.26, -47.88) * mm});
            skCircle(sketch, "E79.16", {"center": v(-60, 60) * mm, "radius": 4 * mm});
            skCircle(sketch, "E79.17", {"center": v(60, 60) * mm, "radius": 4 * mm});
            skCircle(sketch, "E79.18", {"center": v(60, -60) * mm, "radius": 4 * mm});
            skCircle(sketch, "E79.19", {"center": v(-60, -60) * mm, "radius": 4 * mm});
            skLineSegment(sketch, "E80", {"start": v(0, 74.25) * mm, "end": v(0, 104.25) * mm, "construction": true});
            skCircle(sketch, "E81", {"center": v(0, 104.25) * mm, "radius": 6 * mm});
            skLineSegment(sketch, "E82", {"start": v(-15, 92.25) * mm, "end": v(-15, 104.25) * mm});
            skLineSegment(sketch, "E83", {"start": v(15, 92.25) * mm, "end": v(15, 104.25) * mm});
            skArc(sketch, "E84", {"start": v(15, 104.25) * mm, "mid": v(0, 119.25) * mm, "end": v(-15, 104.25) * mm});
            skLineSegment(sketch, "E85", {"start": v(-15, 92.25) * mm, "end": v(-33, 74.25) * mm});
            skLineSegment(sketch, "E86", {"start": v(15, 92.25) * mm, "end": v(33, 74.25) * mm});
            skLineSegment(sketch, "E87", {"start": v(-74.25, 0) * mm, "end": v(74.25, 0) * mm, "construction": true});
            skLineSegment(sketch, "E88.MirrorCS", {"start": v(-15, -92.25) * mm, "end": v(-33, -74.25) * mm});
            skLineSegment(sketch, "E89.MirrorCS", {"start": v(-15, -92.25) * mm, "end": v(-15, -104.25) * mm});
            skArc(sketch, "E90.MirrorCS", {"start": v(15, -104.25) * mm, "mid": v(0, -119.25) * mm, "end": v(-15, -104.25) * mm});
            skCircle(sketch, "E91.MirrorC", {"center": v(0, -104.25) * mm, "radius": 6 * mm});
            skLineSegment(sketch, "E92.MirrorCS", {"start": v(15, -92.25) * mm, "end": v(15, -104.25) * mm});
            skLineSegment(sketch, "E93.MirrorCS", {"start": v(15, -92.25) * mm, "end": v(33, -74.25) * mm});
            skLineSegment(sketch, "E94.MirrorCS", {"start": v(0, -74.25) * mm, "end": v(0, -104.25) * mm, "construction": true});
            skSolve(sketch);
        }
        {
            var Q0;
            Q0=makeQuery(id+"F16.imprint","IMPRINT",FACE,{"disambiguationData":[TD([[makeQuery(id+"F16.imprint","IMPRINT",EDGE,{"derivedFrom":sQuery(id+"F16.wireOp",EDGE,"E81")}),-1.0]])]});
            var Q1;
            Q1=makeQuery(id+"F16.imprint","IMPRINT",FACE,{"disambiguationData":[TD([[makeQuery(id+"F16.imprint","IMPRINT",EDGE,{"derivedFrom":sQuery(id+"F16.wireOp",EDGE,"E79.0")}),-1.0]])]});
            var Q2;
            {var subQ0=sQuery(id+"F16.wireOp",EDGE,"E88.MirrorCS");Q2=makeQuery(id+"F16.imprint","IMPRINT",FACE,{"disambiguationData":[TD([[makeQuery(id+"F16.imprint","IMPRINT",EDGE,{"derivedFrom":subQ0}),-1.0]])]});}
            var Q3;
            {var subQ0=sQuery(id+"F4.wireOp",EDGE,"E36.filletArc");var subQ1=sQuery(id+"F4.wireOp",EDGE,"E35.filletArc");var subQ2=sQuery(id+"F4.wireOp",EDGE,"E34.filletArc");var subQ3=sQuery(id+"F4.wireOp",EDGE,"E33.filletArc");var subQ4=sQuery(id+"F4.wireOp",EDGE,"E27.0");var subQ5=sQuery(id+"F4.wireOp",EDGE,"E30");var subQ6=sQuery(id+"F4.wireOp",EDGE,"E28.0");var subQ7=sQuery(id+"F4.wireOp",EDGE,"E29");Q3=makeQuery(id+"F6.boolean.opBoolean","SPLIT",FACE,{"disambiguationData":[TD([makeQuery(id+"F5.opExtrude","SWEPT_FACE",FACE,{"disambiguationData":[OSD([subQ4])]})])],"derivedFrom":makeQuery(id+"F5.opExtrude","CAP_FACE",FACE,{"disambiguationData":[OSD([subQ4,subQ6,subQ7,subQ5,subQ3,subQ2,subQ1,subQ0,sQuery(id+"F4.wireOp",EDGE,"E41"),sQuery(id+"F4.wireOp",EDGE,"E42"),sQuery(id+"F4.wireOp",EDGE,"E43"),sQuery(id+"F4.wireOp",EDGE,"E45"),sQuery(id+"F4.wireOp",EDGE,"E46"),sQuery(id+"F4.wireOp",EDGE,"E47.filletArc"),sQuery(id+"F4.wireOp",EDGE,"E48.filletArc"),sQuery(id+"F4.wireOp",EDGE,"E49.filletArc"),sQuery(id+"F4.wireOp",EDGE,"E50.filletArc"),sQuery(id+"F4.wireOp",EDGE,"E51.filletArc"),sQuery(id+"F4.wireOp",EDGE,"E52.filletArc"),sQuery(id+"F4.wireOp",EDGE,"E53.0.MirrorCS"),sQuery(id+"F4.wireOp",EDGE,"E54.0.MirrorCS"),sQuery(id+"F4.wireOp",EDGE,"E55.0.MirrorCS"),sQuery(id+"F4.wireOp",EDGE,"E56.0.MirrorCS"),sQuery(id+"F4.wireOp",EDGE,"E57.0.MirrorCS"),sQuery(id+"F4.wireOp",EDGE,"E58.0.MirrorCS"),sQuery(id+"F4.wireOp",EDGE,"E59.0.MirrorCS"),sQuery(id+"F4.wireOp",EDGE,"E60.0.MirrorCS"),sQuery(id+"F4.wireOp",EDGE,"E61.0.MirrorCS"),sQuery(id+"F4.wireOp",EDGE,"E62.0.MirrorCS"),sQuery(id+"F4.wireOp",EDGE,"E63.0.MirrorCS")])],"isStart":true})});}
            extrude(context, id + "F17", {"entities" : qUnion([Q0, Q1, Q2]), "endBound" : BoundingType.UP_TO_SURFACE, "depth" : 25 * mm, "endBoundEntityFace" : qUnion([Q3]), "offsetDistance" : 25 * mm});
        }
    });
